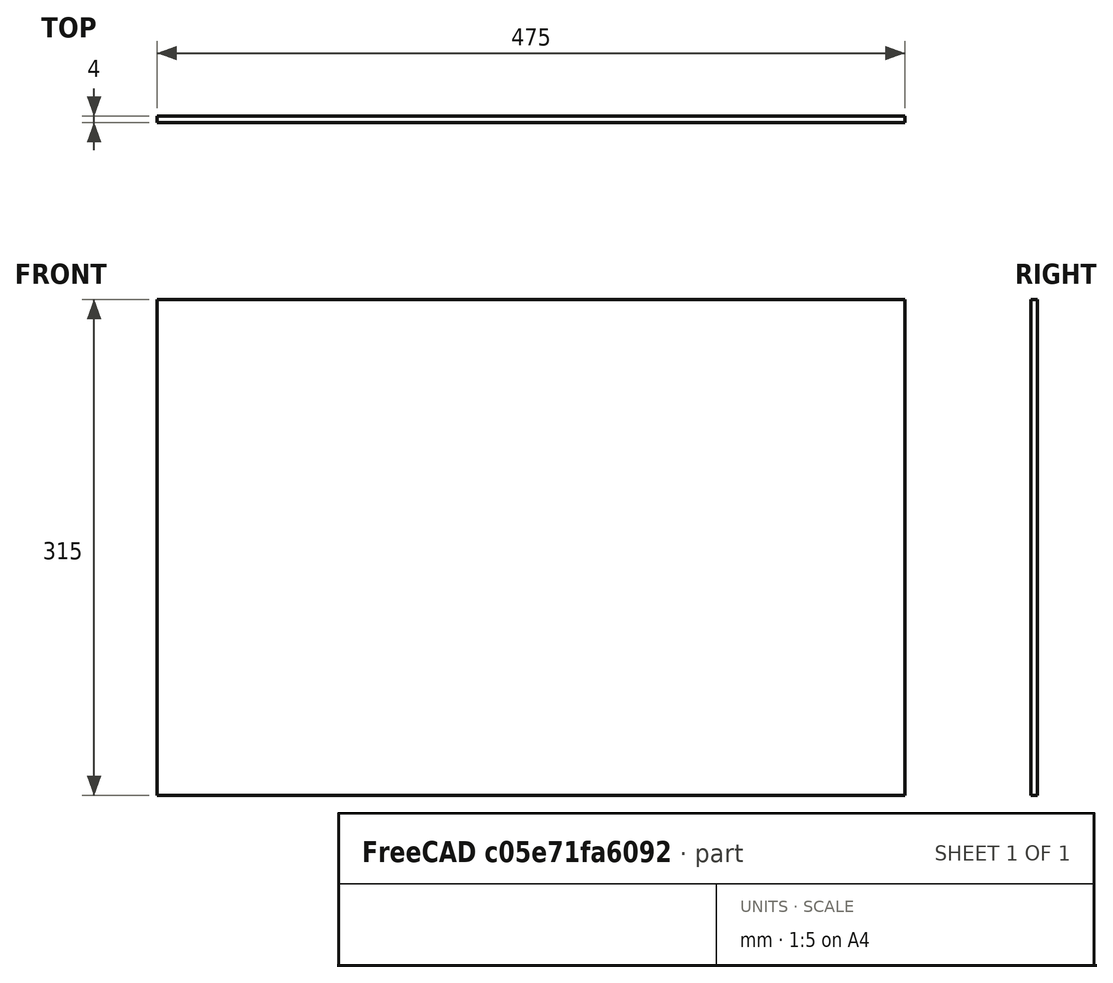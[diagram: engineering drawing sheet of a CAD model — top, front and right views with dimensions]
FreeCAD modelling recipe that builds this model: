
FCSTD DOCUMENT  (FreeCAD 0.18R4 (GitTag))
Label: side_glass
License: All rights reserved
LicenseURL: http://en.wikipedia.org/wiki/All_rights_reserved
objects: Sketcher::SketchObject×1, PartDesign::Pad×1, PartDesign::Body×1
note: 4 computed .brp shape members not serialized (recipe doc carries the construction recipe); baked Part::Feature solids carry a one-line shape summary decoded from their .brp

FEATURE [Sketcher::SketchObject] Sketch
  MapMode = 5
  Placement = pos=(0,0,0) rot=(1,0,0;1.5708rad)
  Support = -> [XZ_Plane]
  sketch-geometry (4):
    g0: LineSegment StartX=0 StartY=0 StartZ=0 EndX=-475 EndY=0 EndZ=0
    g1: LineSegment StartX=-475 StartY=0 StartZ=0 EndX=-475 EndY=315 EndZ=0
    g2: LineSegment StartX=-475 StartY=315 StartZ=0 EndX=0 EndY=315 EndZ=0
    g3: LineSegment StartX=0 StartY=315 StartZ=0 EndX=0 EndY=0 EndZ=0
  constraints (11):
    c: Coincident(g0,g1)
    c: Coincident(g1,g2)
    c: Coincident(g2,g3)
    c: Coincident(g3,g0)
    c: Horizontal(g0)
    c: Horizontal(g2)
    c: Vertical(g1)
    c: Vertical(g3)
    c: Coincident(g0,g-1)
    c: DistanceX(g0,g0) = 475
    c: DistanceY(g3,g3) = 315
FEATURE [PartDesign::Pad] Pad
  Length = 4
  Length2 = 100
  Placement = pos=(0,0,0) rot=(1,0,0;1.5708rad)
  Profile = -> Sketch
  Type = 0
FEATURE [PartDesign::Body] Body
  Group = -> [Sketch,Pad]
  Origin = -> Origin
  Tip = -> Pad
